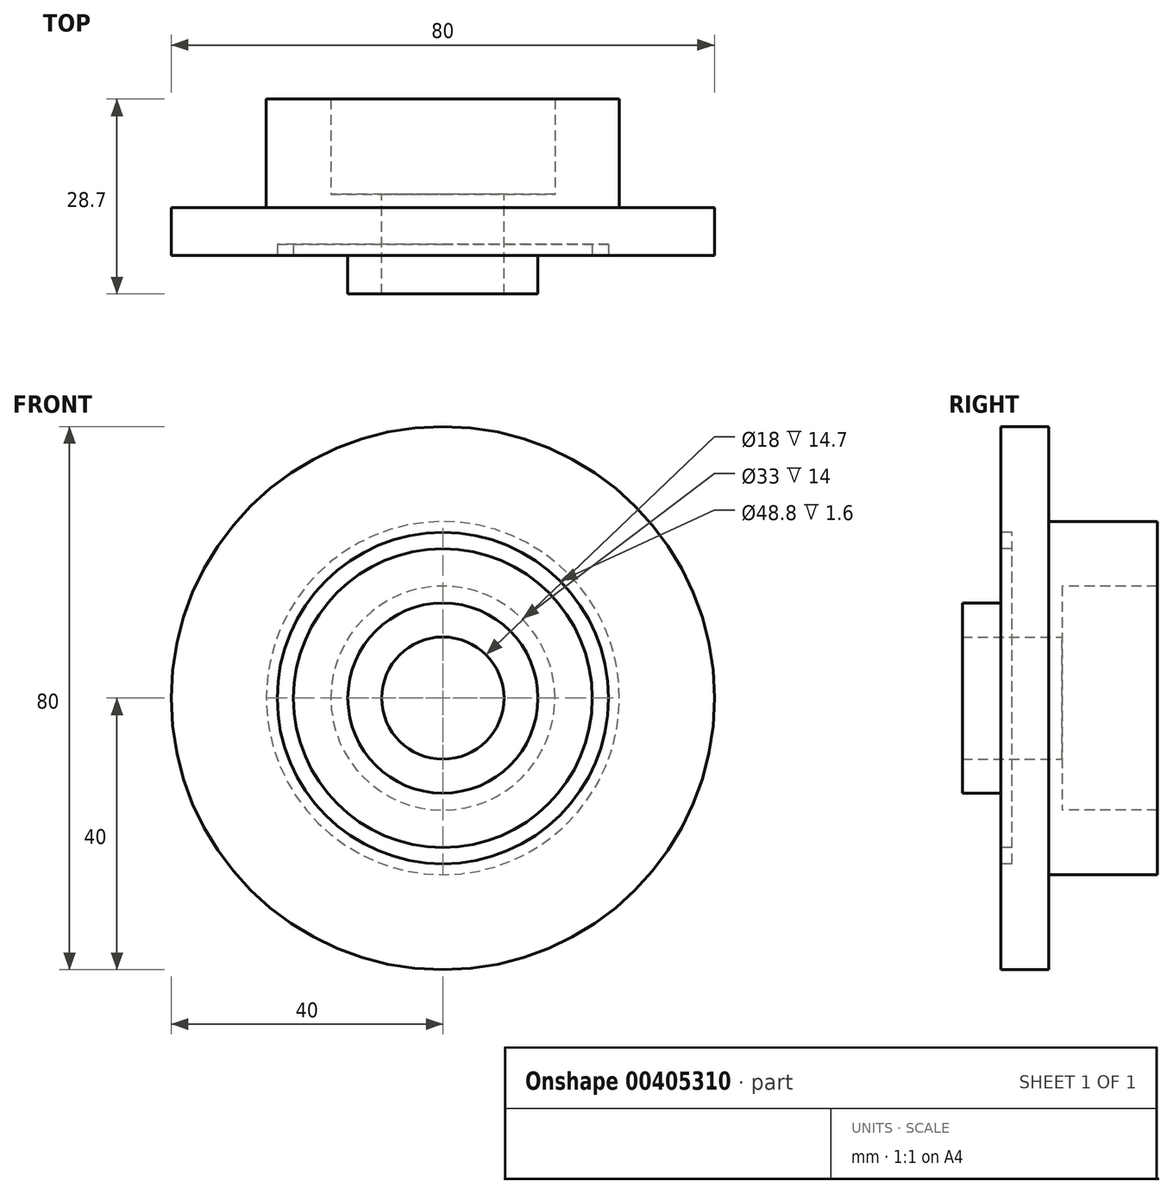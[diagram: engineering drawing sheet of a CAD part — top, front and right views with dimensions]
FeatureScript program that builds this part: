
annotation { "Feature Type Name" : "Feature", "Feature Type Description" : "" }
export const myFeature = defineFeature(function(context is Context, id is Id, definition is map)
    precondition{}
    {
        {
            var Q0;
            Q0=qCreatedBy(makeId("Front.planeOp"),FACE);
            var sketch = newSketch(context, id + "F0", { "sketchPlane" : qUnion([Q0])});
            skCircle(sketch, "E0", {"center": v(0, 0) * mm, "radius": 9 * mm});
            skCircle(sketch, "E1", {"center": v(0, 0) * mm, "radius": 40 * mm});
            skSolve(sketch);
        }
        {
            var Q0;
            Q0 = qSketchRegion(id + "F0", true);
            extrude(context, id + "F1", {"entities" : qUnion([Q0]), "depth" : 7 * mm});
        }
        {
            var Q0;
            Q0=makeQuery(id+"F1.opExtrude","CAP_FACE",FACE,{"disambiguationData":[OSD([sQuery(id+"F0.wireOp",EDGE,"E0"),sQuery(id+"F0.wireOp",EDGE,"E1")])],"isStart":false});
            var sketch = newSketch(context, id + "F2", { "sketchPlane" : qUnion([Q0])});
            skCircle(sketch, "E2", {"center": v(0, 0) * mm, "radius": 9 * mm});
            skCircle(sketch, "E3", {"center": v(0, 0) * mm, "radius": 14 * mm});
            skSolve(sketch);
        }
        {
            var Q0;
            Q0 = qSketchRegion(id + "F2", true);
            extrude(context, id + "F3", {"entities" : qUnion([Q0]), "operationType" : NewBodyOperationType.ADD, "depth" : 10 * mm});
        }
        {
            var Q0;
            Q0=makeQuery(id+"F3.opExtrude","CAP_FACE",FACE,{"disambiguationData":[OSD([sQuery(id+"F2.wireOp",EDGE,"E2"),sQuery(id+"F2.wireOp",EDGE,"E3")])],"isStart":false});
            var sketch = newSketch(context, id + "F4", { "sketchPlane" : qUnion([Q0])});
            skCircle(sketch, "E4", {"center": v(0, 0) * mm, "radius": 12.5 * mm});
            skSolve(sketch);
        }
        {
            var Q0;
            Q0 = qSketchRegion(id + "F4", true);
            extrude(context, id + "F5", {"entities" : qUnion([Q0]), "operationType" : NewBodyOperationType.REMOVE, "oppositeDirection" : true, "depth" : 4.2 * mm});
        }
        {
            var Q0;
            Q0=makeQuery(id+"F1.opExtrude","CAP_FACE",FACE,{"disambiguationData":[OSD([sQuery(id+"F0.wireOp",EDGE,"E0"),sQuery(id+"F0.wireOp",EDGE,"E1")])],"isStart":true});
            var sketch = newSketch(context, id + "F6", { "sketchPlane" : qUnion([Q0])});
            skCircle(sketch, "E5", {"center": v(0, 0) * mm, "radius": 9 * mm});
            skCircle(sketch, "E6", {"center": v(0, 0) * mm, "radius": 26 * mm});
            skSolve(sketch);
        }
        {
            var Q0;
            Q0 = qSketchRegion(id + "F6", true);
            extrude(context, id + "F7", {"entities" : qUnion([Q0]), "operationType" : NewBodyOperationType.ADD, "depth" : 2 * mm});
        }
        {
            var Q0;
            Q0=makeQuery(id+"F7.opExtrude","CAP_FACE",FACE,{"disambiguationData":[OSD([sQuery(id+"F6.wireOp",EDGE,"E5"),sQuery(id+"F6.wireOp",EDGE,"E6")])],"isStart":false});
            var sketch = newSketch(context, id + "F8", { "sketchPlane" : qUnion([Q0])});
            skCircle(sketch, "E7", {"center": v(0, 0) * mm, "radius": 16.5 * mm});
            skCircle(sketch, "E8", {"center": v(0, 0) * mm, "radius": 26 * mm});
            skSolve(sketch);
        }
        {
            var Q0;
            Q0 = qSketchRegion(id + "F8", true);
            extrude(context, id + "F9", {"entities" : qUnion([Q0]), "operationType" : NewBodyOperationType.ADD, "depth" : 14 * mm});
        }
        {
            var Q0;
            Q0=makeQuery(id+"F1.opExtrude","CAP_FACE",FACE,{"disambiguationData":[OSD([sQuery(id+"F0.wireOp",EDGE,"E0"),sQuery(id+"F0.wireOp",EDGE,"E1")])],"isStart":false});
            var sketch = newSketch(context, id + "F10", { "sketchPlane" : qUnion([Q0])});
            skCircle(sketch, "E9", {"center": v(0, 0) * mm, "radius": 19 * mm});
            skCircle(sketch, "E10", {"center": v(0, 0) * mm, "radius": 33 * mm});
            skSolve(sketch);
        }
        {
            var Q0;
            Q0=makeQuery(id+"F3.opExtrude","CAP_FACE",FACE,{"disambiguationData":[OSD([sQuery(id+"F2.wireOp",EDGE,"E2"),sQuery(id+"F2.wireOp",EDGE,"E3")])],"isStart":false});
            var sketch = newSketch(context, id + "F11", { "sketchPlane" : qUnion([Q0])});
            skCircle(sketch, "E11", {"center": v(0, 0) * mm, "radius": 14 * mm});
            skSolve(sketch);
        }
        {
            var Q0;
            Q0 = qSketchRegion(id + "F11", true);
            extrude(context, id + "F12", {"entities" : qUnion([Q0]), "operationType" : NewBodyOperationType.REMOVE, "oppositeDirection" : true, "depth" : 4.3 * mm});
        }
        {
            var Q0;
            Q0=qCreatedBy(makeId("Top.planeOp"),FACE);
            var sketch = newSketch(context, id + "F13", { "sketchPlane" : qUnion([Q0])});
            skLineSegment(sketch, "E12.bottom", {"start": v(22, -7) * mm, "end": v(24.4, -7) * mm});
            skLineSegment(sketch, "E12.top", {"start": v(22, -5.4) * mm, "end": v(24.4, -5.4) * mm});
            skLineSegment(sketch, "E12.left", {"start": v(22, -7) * mm, "end": v(22, -5.4) * mm});
            skLineSegment(sketch, "E12.right", {"start": v(24.4, -7) * mm, "end": v(24.4, -5.4) * mm});
            skLineSegment(sketch, "E13", {"start": v(22, -7) * mm, "end": v(0, -7) * mm});
            skLineSegment(sketch, "E14", {"start": v(24.4, -5.4) * mm, "end": v(0, -5.4) * mm});
            skSolve(sketch);
        }
        {
            var Q0;
            Q0=makeQuery(id+"F1.opExtrude","SWEPT_BODY",BODY,{"disambiguationData":[OSD([sQuery(id+"F0.wireOp",EDGE,"E0"),sQuery(id+"F0.wireOp",EDGE,"E1")])]});
            transform(context, id + "F14", {"entities" : qUnion([Q0]), "transformType" : TransformType.TRANSLATION_3D, "dx" : 0 * mm, "dy" : 0 * mm, "dz" : 110.7 * mm, "makeCopy" : true});
        }
        {
            var Q0;
            Q0=makeQuery(id+"F14.opPattern","COPY",BODY,{"derivedFrom":makeQuery(id+"F1.opExtrude","SWEPT_BODY",BODY,{"disambiguationData":[OSD([sQuery(id+"F0.wireOp",EDGE,"E0"),sQuery(id+"F0.wireOp",EDGE,"E1")])]}),"instanceName":"1"});
            deleteBodies(context, id + "F15", {"entities" : qUnion([Q0])});
        }
        {
            var Q0;
            Q0 = qSketchRegion(id + "F13", true);
            var Q1;
            Q1=makeQuery(id+"F1.opExtrude","CAP_EDGE",EDGE,{"disambiguationData":[OSD([sQuery(id+"F0.wireOp",EDGE,"E1")])],"isStart":false});
            revolve(context, id + "F16", {"operationType" : NewBodyOperationType.REMOVE, "entities" : qUnion([Q0]), "axis" : qUnion([Q1]), "revolveType" : RevolveType.FULL, "oppositeDirection" : true});
        }
    });
